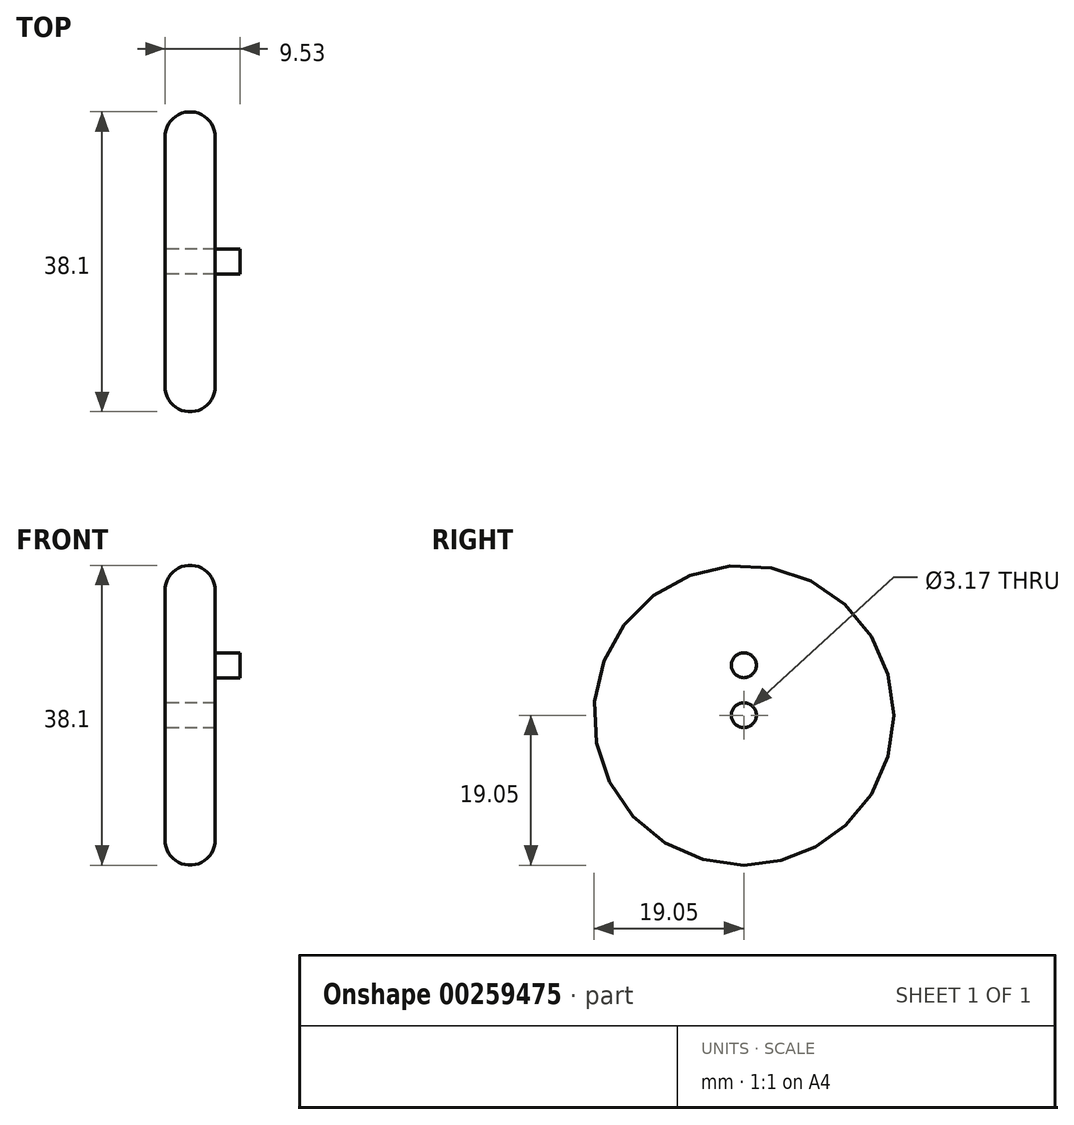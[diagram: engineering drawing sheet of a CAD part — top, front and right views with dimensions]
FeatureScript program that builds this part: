
annotation { "Feature Type Name" : "Feature", "Feature Type Description" : "" }
export const myFeature = defineFeature(function(context is Context, id is Id, definition is map)
    precondition{}
    {
        {
            var Q0;
            Q0=qCreatedBy(makeId("Right.planeOp"),FACE);
            var sketch = newSketch(context, id + "F0", { "sketchPlane" : qUnion([Q0])});
            skCircle(sketch, "E0", {"center": v(0, 0) * mm, "radius": 19.05 * mm});
            skSolve(sketch);
        }
        {
            var Q0;
            Q0=makeQuery(id+"F0.imprint","IMPRINT",FACE,{"disambiguationData":[TD([[makeQuery(id+"F0.imprint","IMPRINT",EDGE,{"derivedFrom":sQuery(id+"F0.wireOp",EDGE,"E0")}),1.0]])]});
            var sketch = newSketch(context, id + "F1", { "sketchPlane" : qUnion([Q0])});
            skCircle(sketch, "E1", {"center": v(0, 0) * mm, "radius": 1.59 * mm});
            skSolve(sketch);
        }
        {
            var Q0;
            Q0=makeQuery(id+"F0.imprint","IMPRINT",FACE,{"disambiguationData":[TD([[makeQuery(id+"F0.imprint","IMPRINT",EDGE,{"derivedFrom":sQuery(id+"F0.wireOp",EDGE,"E0")}),1.0]])]});
            var sketch = newSketch(context, id + "F2", { "sketchPlane" : qUnion([Q0])});
            skCircle(sketch, "E2", {"center": v(0, 0) * mm, "radius": 1.59 * mm});
            skSolve(sketch);
        }
        {
            var Q0;
            Q0=makeQuery(id+"F0.imprint","IMPRINT",FACE,{"disambiguationData":[TD([[makeQuery(id+"F0.imprint","IMPRINT",EDGE,{"derivedFrom":sQuery(id+"F0.wireOp",EDGE,"E0")}),1.0]])]});
            extrude(context, id + "F3", {"entities" : qUnion([Q0]), "depth" : 6.35 * mm});
        }
        {
            var Q0;
            Q0=makeQuery(id+"F2.imprint","IMPRINT",FACE,{"disambiguationData":[TD([[makeQuery(id+"F2.imprint","IMPRINT",EDGE,{"derivedFrom":sQuery(id+"F2.wireOp",EDGE,"E2")}),1.0]])]});
            extrude(context, id + "F4", {"entities" : qUnion([Q0]), "operationType" : NewBodyOperationType.REMOVE, "depth" : 6.35 * mm});
        }
        {
            var Q0;
            Q0=makeQuery(id+"F3.opExtrude","CAP_EDGE",EDGE,{"disambiguationData":[OSD([sQuery(id+"F0.wireOp",EDGE,"E0")])],"isStart":true});
            fillet(context, id + "F5", {"entities" : qUnion([Q0]), "radius" : 3.17 * mm, "tangentPropagation" : true, "allowEdgeOverflow" : false});
        }
        {
            var Q0;
            Q0=makeQuery(id+"F3.opExtrude","CAP_EDGE",EDGE,{"disambiguationData":[OSD([sQuery(id+"F0.wireOp",EDGE,"E0")])],"isStart":false});
            fillet(context, id + "F6", {"entities" : qUnion([Q0]), "radius" : 3.17 * mm, "tangentPropagation" : true, "allowEdgeOverflow" : false});
        }
        {
            var Q0;
            Q0=makeQuery(id+"F3.opExtrude","CAP_FACE",FACE,{"disambiguationData":[OSD([sQuery(id+"F0.wireOp",EDGE,"E0")])],"isStart":false});
            var sketch = newSketch(context, id + "F7", { "sketchPlane" : qUnion([Q0])});
            skCircle(sketch, "E3", {"center": v(0, 6.35) * mm, "radius": 1.59 * mm});
            skSolve(sketch);
        }
        {
            var Q0;
            Q0=makeQuery(id+"F7.imprint","IMPRINT",FACE,{"disambiguationData":[TD([[makeQuery(id+"F7.imprint","IMPRINT",EDGE,{"derivedFrom":sQuery(id+"F7.wireOp",EDGE,"E3")}),1.0]])]});
            extrude(context, id + "F8", {"entities" : qUnion([Q0]), "operationType" : NewBodyOperationType.ADD, "depth" : 3.17 * mm});
        }
    });
